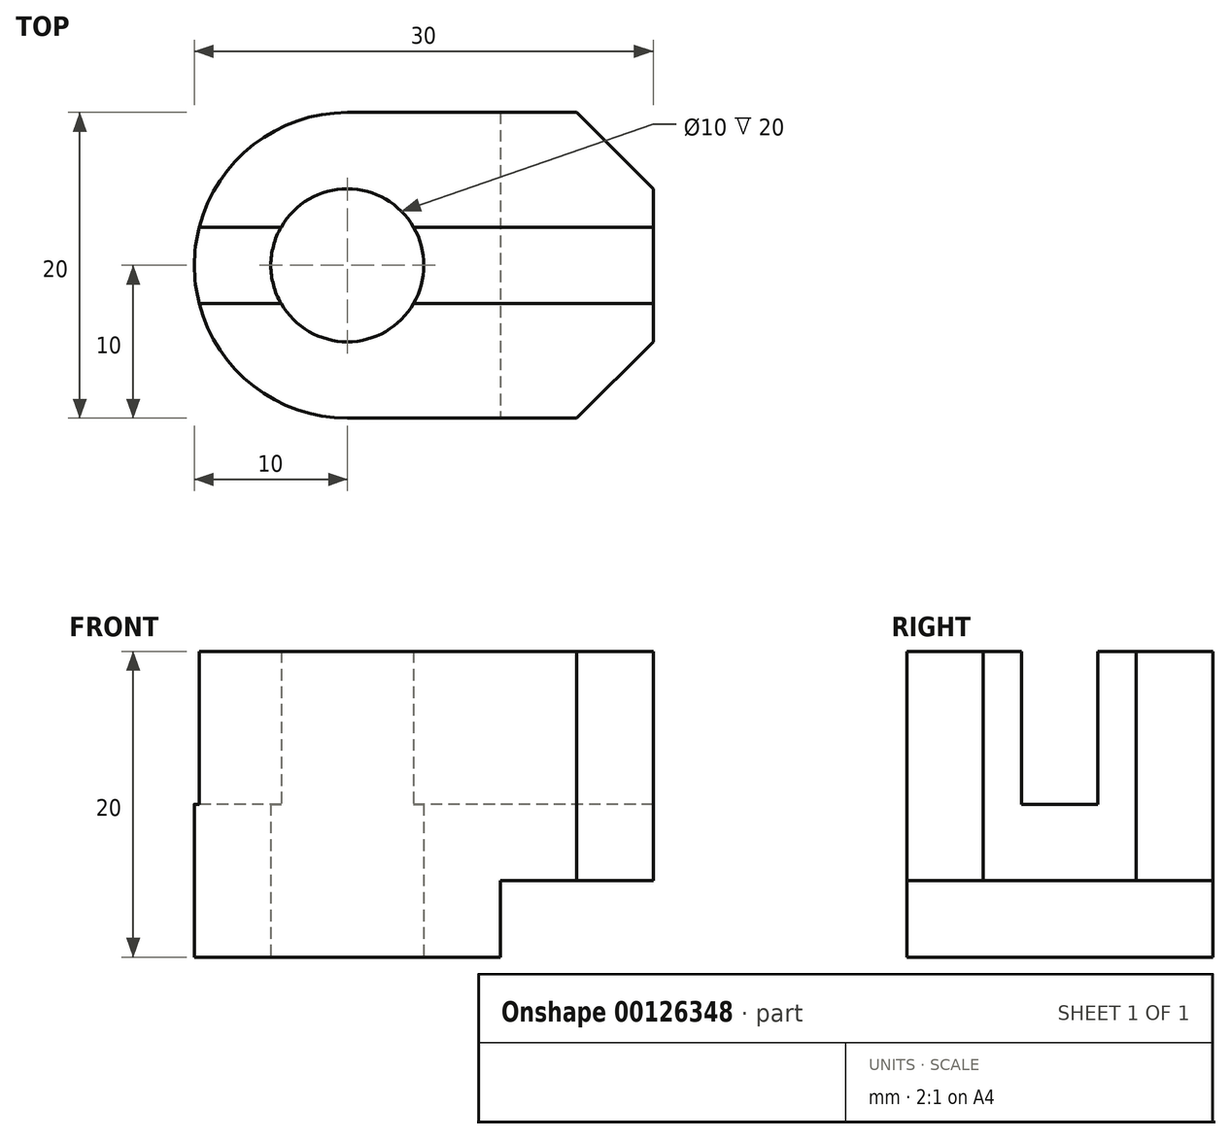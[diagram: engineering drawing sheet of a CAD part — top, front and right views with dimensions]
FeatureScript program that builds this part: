
annotation { "Feature Type Name" : "Feature", "Feature Type Description" : "" }
export const myFeature = defineFeature(function(context is Context, id is Id, definition is map)
    precondition{}
    {
        {
            var Q0;
            Q0=qCreatedBy(makeId("Top.planeOp"),FACE);
            var sketch = newSketch(context, id + "F0", { "sketchPlane" : qUnion([Q0])});
            skCircle(sketch, "E0", {"center": v(0, 0) * mm, "radius": 5 * mm});
            skCircle(sketch, "E1", {"center": v(0, 0) * mm, "radius": 10 * mm});
            skLineSegment(sketch, "E2", {"start": v(0, -10) * mm, "end": v(15, -10) * mm});
            skLineSegment(sketch, "E3", {"start": v(15, -10) * mm, "end": v(20, -5) * mm});
            skLineSegment(sketch, "E4", {"start": v(0, 10) * mm, "end": v(15, 10) * mm});
            skLineSegment(sketch, "E5", {"start": v(15, 10) * mm, "end": v(20, 5) * mm});
            skLineSegment(sketch, "E6", {"start": v(20, -5) * mm, "end": v(20, 5) * mm});
            skSolve(sketch);
        }
        {
            var Q0;
            Q0 = qSketchRegion(id + "F0", true);
            extrude(context, id + "F1", {"entities" : qUnion([Q0]), "depth" : 15 * mm});
        }
        {
            var Q0;
            Q0=makeQuery(id+"F1.opExtrude","CAP_FACE",FACE,{"disambiguationData":[OSD([sQuery(id+"F0.wireOp",EDGE,"E0"),sQuery(id+"F0.wireOp",EDGE,"E1"),sQuery(id+"F0.wireOp",EDGE,"E2"),sQuery(id+"F0.wireOp",EDGE,"E3"),sQuery(id+"F0.wireOp",EDGE,"E4"),sQuery(id+"F0.wireOp",EDGE,"E5"),sQuery(id+"F0.wireOp",EDGE,"E6")])],"isStart":true});
            var sketch = newSketch(context, id + "F2", { "sketchPlane" : qUnion([Q0])});
            skArc(sketch, "E7.0", {"start": v(0, -10) * mm, "mid": v(-10, 0) * mm, "end": v(0, 10) * mm});
            skLineSegment(sketch, "E8", {"start": v(0, -10) * mm, "end": v(10, -10) * mm});
            skLineSegment(sketch, "E9", {"start": v(10, -10) * mm, "end": v(10, 10) * mm});
            skLineSegment(sketch, "E10", {"start": v(10, 10) * mm, "end": v(0, 10) * mm});
            skSolve(sketch);
        }
        {
            var Q0;
            Q0 = qSketchRegion(id + "F2", true);
            extrude(context, id + "F3", {"entities" : qUnion([Q0]), "operationType" : NewBodyOperationType.ADD, "depth" : 5 * mm});
        }
        {
            var Q0;
            Q0=makeQuery(id+"F3.opExtrude","CAP_FACE",FACE,{"disambiguationData":[OSD([sQuery(id+"F2.wireOp",EDGE,"E7.0"),sQuery(id+"F2.wireOp",EDGE,"E8"),sQuery(id+"F2.wireOp",EDGE,"E9"),sQuery(id+"F2.wireOp",EDGE,"E10")])],"isStart":true});
            extrude(context, id + "F4", {"entities" : qUnion([Q0]), "operationType" : NewBodyOperationType.REMOVE, "oppositeDirection" : true, "depth" : 25 * mm});
        }
        {
            var Q0;
            Q0=makeQuery(id+"F1.opExtrude","CAP_FACE",FACE,{"disambiguationData":[OSD([sQuery(id+"F0.wireOp",EDGE,"E0"),sQuery(id+"F0.wireOp",EDGE,"E1"),sQuery(id+"F0.wireOp",EDGE,"E2"),sQuery(id+"F0.wireOp",EDGE,"E3"),sQuery(id+"F0.wireOp",EDGE,"E4"),sQuery(id+"F0.wireOp",EDGE,"E5"),sQuery(id+"F0.wireOp",EDGE,"E6")])],"isStart":false});
            var sketch = newSketch(context, id + "F5", { "sketchPlane" : qUnion([Q0])});
            skLineSegment(sketch, "E11", {"start": v(-9.68, -2.5) * mm, "end": v(20, -2.5) * mm});
            skLineSegment(sketch, "E12", {"start": v(20, -2.5) * mm, "end": v(20, 2.5) * mm});
            skLineSegment(sketch, "E13", {"start": v(20, 2.5) * mm, "end": v(-9.68, 2.5) * mm});
            skArc(sketch, "E14", {"start": v(-9.68, 2.5) * mm, "mid": v(-10, 0) * mm, "end": v(-9.68, -2.5) * mm});
            skSolve(sketch);
        }
        {
            var Q0;
            Q0 = qSketchRegion(id + "F5", true);
            extrude(context, id + "F6", {"entities" : qUnion([Q0]), "operationType" : NewBodyOperationType.REMOVE, "oppositeDirection" : true, "depth" : 10 * mm});
        }
    });
